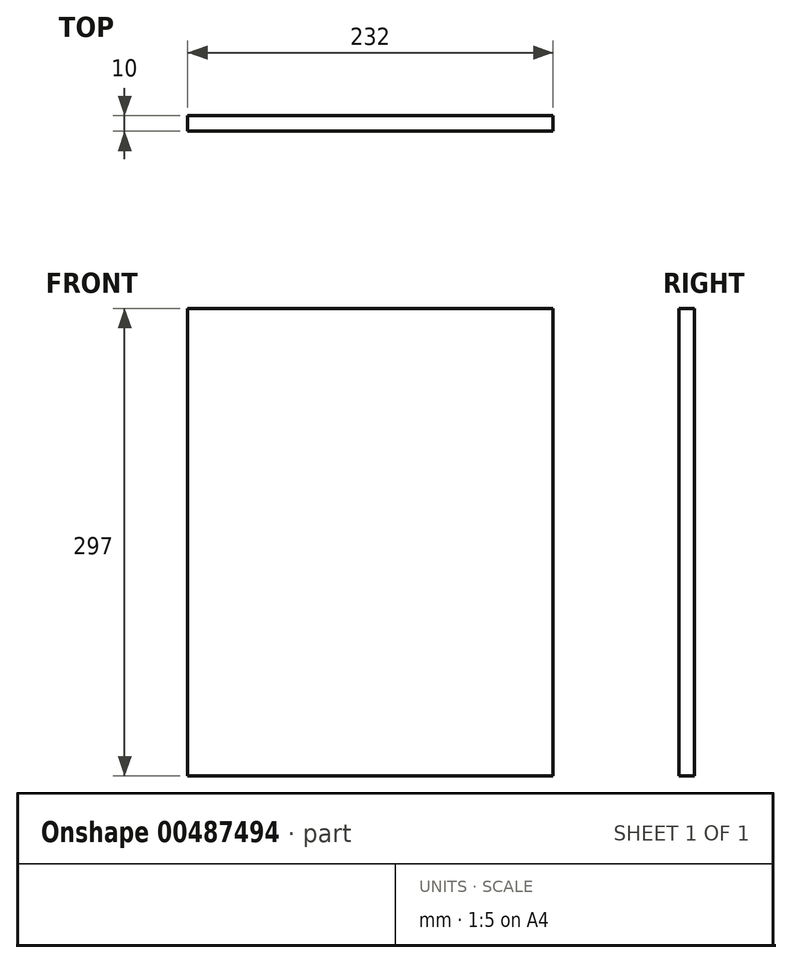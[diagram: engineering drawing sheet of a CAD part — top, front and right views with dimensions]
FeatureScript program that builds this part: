
annotation { "Feature Type Name" : "Feature", "Feature Type Description" : "" }
export const myFeature = defineFeature(function(context is Context, id is Id, definition is map)
    precondition{}
    {
        {
            var Q0;
            Q0=qCreatedBy(makeId("Front.planeOp"),FACE);
            var sketch = newSketch(context, id + "F0", { "sketchPlane" : qUnion([Q0])});
            skLineSegment(sketch, "E0.bottom", {"start": v(116, 148.5) * mm, "end": v(-116, 148.5) * mm});
            skLineSegment(sketch, "E0.top", {"start": v(116, -148.5) * mm, "end": v(-116, -148.5) * mm});
            skLineSegment(sketch, "E0.left", {"start": v(116, 148.5) * mm, "end": v(116, -148.5) * mm});
            skLineSegment(sketch, "E0.right", {"start": v(-116, 148.5) * mm, "end": v(-116, -148.5) * mm});
            skPoint(sketch, "E0.middle", {"position": v(0, 0) * mm});
            skSolve(sketch);
        }
        {
            var Q0;
            Q0 = qSketchRegion(id + "F0", true);
            extrude(context, id + "F1", {"entities" : qUnion([Q0]), "depth" : 10 * mm});
        }
    });
